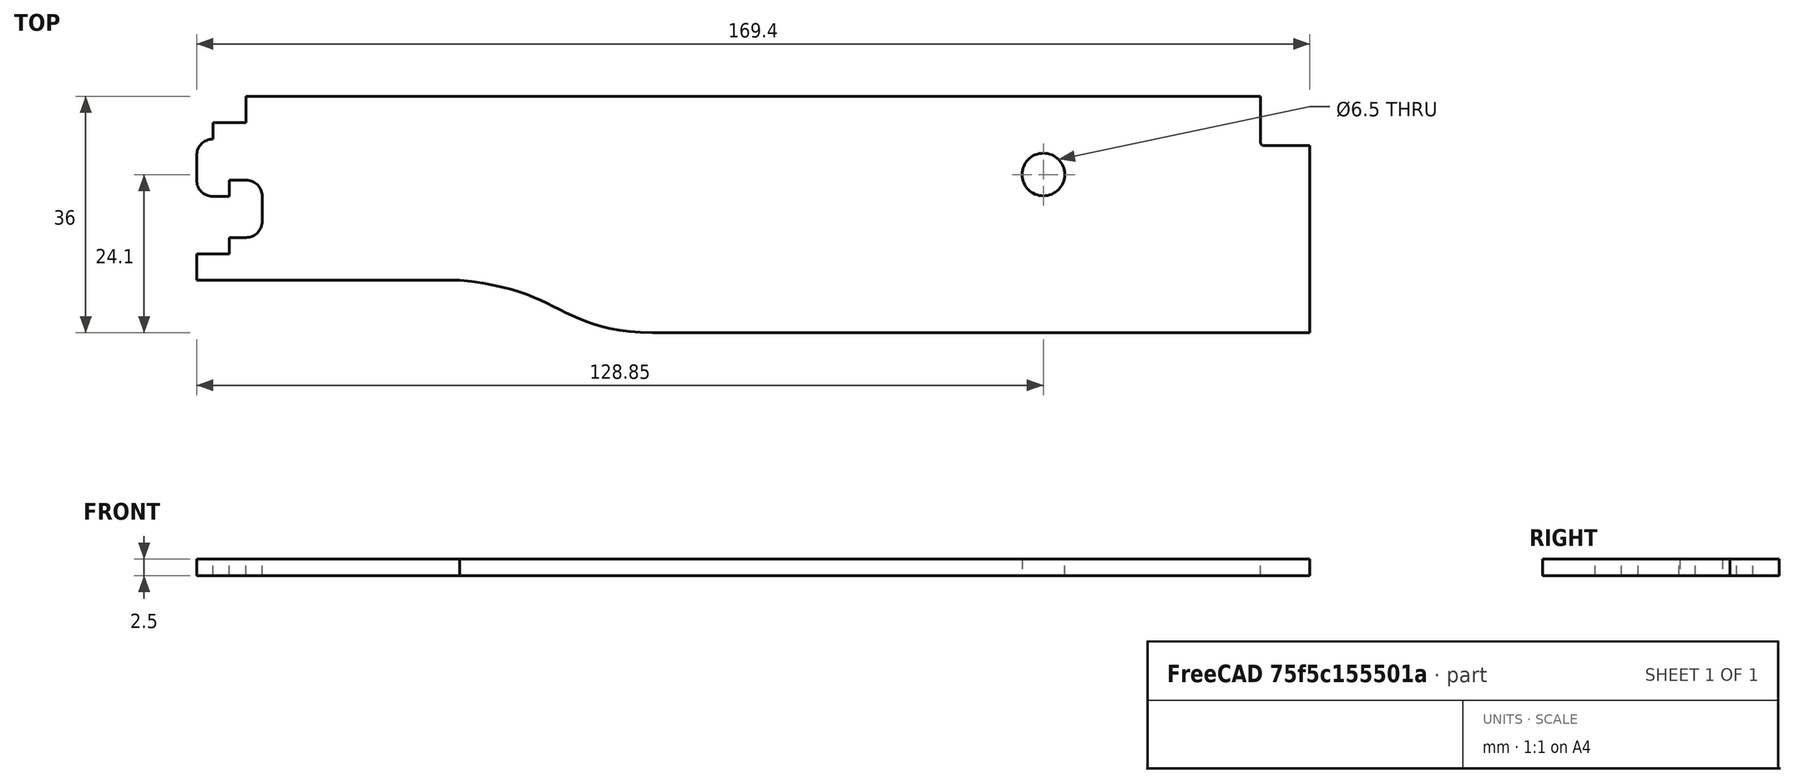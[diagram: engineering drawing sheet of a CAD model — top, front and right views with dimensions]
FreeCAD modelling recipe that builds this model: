
FCSTD DOCUMENT  (FreeCAD 0.19R0.19.2)
Label: v0_14
License: All rights reserved
LicenseURL: http://en.wikipedia.org/wiki/All_rights_reserved
objects: Sketcher::SketchObject×2, Part::Extrusion×1
note: 3 computed .brp shape members not serialized (recipe doc carries the construction recipe); baked Part::Feature solids carry a one-line shape summary decoded from their .brp

FEATURE [Sketcher::SketchObject] Sketch
  FullyConstrained = true
  sketch-geometry (33):
    g0: LineSegment StartX=0 StartY=0 StartZ=0 EndX=154.4 EndY=0 EndZ=0
    g1: LineSegment StartX=154.4 StartY=0 StartZ=0 EndX=154.4 EndY=-7 EndZ=0
    g2: LineSegment StartX=154.9 StartY=-7.5 StartZ=0 EndX=161.9 EndY=-7.5 EndZ=0
    g3: ArcOfCircle CenterX=154.9 CenterY=-7 CenterZ=0 NormalX=0 NormalY=0 NormalZ=1 AngleXU=0 Radius=0.5 StartAngle=3.14159 EndAngle=4.71239
    g4: Circle CenterX=121.35 CenterY=-11.9 CenterZ=0 NormalX=0 NormalY=0 NormalZ=1 AngleXU=0 Radius=3.25
    g5: LineSegment StartX=0 StartY=0 StartZ=0 EndX=0 EndY=-4 EndZ=0
    g6: LineSegment StartX=-5 StartY=-4 StartZ=0 EndX=0 EndY=-4 EndZ=0
    g7: LineSegment StartX=-5 StartY=-4 StartZ=0 EndX=-5 EndY=-6.5 EndZ=0
    g8: LineSegment StartX=-7.5 StartY=-9 StartZ=0 EndX=-7.5 EndY=-12.75 EndZ=0
    g9: ArcOfCircle CenterX=-5 CenterY=-9 CenterZ=0 NormalX=0 NormalY=0 NormalZ=1 AngleXU=0 Radius=2.5 StartAngle=1.5708 EndAngle=3.14159
    g10: LineSegment StartX=-5 StartY=-15.25 StartZ=0 EndX=-2.5 EndY=-15.25 EndZ=0
    g11: ArcOfCircle CenterX=-5 CenterY=-12.75 CenterZ=0 NormalX=0 NormalY=0 NormalZ=1 AngleXU=0 Radius=2.5 StartAngle=3.14159 EndAngle=4.71239
    g12: LineSegment StartX=-2.5 StartY=-15.25 StartZ=0 EndX=-2.5 EndY=-12.75 EndZ=0
    g13: LineSegment StartX=-2.5 StartY=-12.75 StartZ=0 EndX=1.488e-13 EndY=-12.75 EndZ=0
    g14: ArcOfCircle CenterX=1.486e-13 CenterY=-15.25 CenterZ=0 NormalX=0 NormalY=0 NormalZ=1 AngleXU=0 Radius=2.5 StartAngle=8e-16 EndAngle=1.5708
    g15: LineSegment StartX=2.5 StartY=-15.25 StartZ=0 EndX=2.5 EndY=-19 EndZ=0
    g16: ArcOfCircle CenterX=1.483e-13 CenterY=-19 CenterZ=0 NormalX=0 NormalY=0 NormalZ=1 AngleXU=0 Radius=2.5 StartAngle=4.71239 EndAngle=6.28319
    g17: LineSegment StartX=-2.5 StartY=-21.5 StartZ=0 EndX=1.479e-13 EndY=-21.5 EndZ=0
    g18: LineSegment StartX=-2.5 StartY=-21.5 StartZ=0 EndX=-2.5 EndY=-24 EndZ=0
    g19: LineSegment StartX=-7.5 StartY=-24 StartZ=0 EndX=-2.5 EndY=-24 EndZ=0
    g20: LineSegment StartX=-7.5 StartY=-24 StartZ=0 EndX=-7.5 EndY=-28 EndZ=0
    g21: LineSegment StartX=161.9 StartY=-7.5 StartZ=0 EndX=161.9 EndY=-36 EndZ=0
    g22: LineSegment StartX=61.85 StartY=-36 StartZ=0 EndX=161.9 EndY=-36 EndZ=0
    g23-g27: Circle x5 (B-spline internal-alignment scaffolding for g28; pole/knot coordinates omitted)
    g28: BSplineCurve PolesCount=5 KnotsCount=3 Degree=3 IsPeriodic=0
    g29: GeomPoint X=61.85 Y=-36 Z=0
    g30: GeomPoint X=47.2264 Y=-32.2128 Z=0
    g31: GeomPoint X=32.5209 Y=-28 Z=0
    g32: LineSegment StartX=32.5209 StartY=-28 StartZ=0 EndX=-7.5 EndY=-28 EndZ=0
  constraints (75):
    c: PointOnObject(g0,g-2)
    c: Horizontal(g0)
    c: Distance(g0) = 154.4
    c: DistanceY(g-1,g0) = 0
    c: Vertical(g1)
    c: Distance(g1) = 7
    c: Coincident(g1,g0)
    c: Horizontal(g2)
    c: Distance(g2) = 7
    c: Coincident(g3,g1)
    c: Tangent(g2,g3)
    c: Tangent(g2,g3,g2) = -1.5708
    c: Block(g3)
    c: Block(g4)
    c: Vertical(g5)
    c: Distance(g5) = 4
    c: Coincident(g5,g0)
    c: Horizontal(g6)
    c: Distance(g6) = 5
    c: Coincident(g6,g5)
    c: Vertical(g7)
    c: Distance(g7) = 2.5
    c: Coincident(g7,g6)
    c: Vertical(g8)
    c: Distance(g8) = 3.75
    c: Coincident(g9,g7)
    c: Block(g9)
    c: Coincident(g8,g9)
    c: Horizontal(g10)
    c: Distance(g10) = 2.5
    c: Coincident(g11,g8)
    c: Block(g11)
    c: Block(g10)
    c: Vertical(g12)
    c: Distance(g12) = 2.5
    c: Coincident(g12,g10)
    c: Horizontal(g13)
    c: Distance(g13) = 2.5
    c: Coincident(g13,g12)
    c: Coincident(g14,g13)
    c: Vertical(g15)
    c: Distance(g15) = 3.75
    c: Block(g14)
    c: Coincident(g15,g14)
    c: Coincident(g16,g15)
    c: Block(g16)
    c: Horizontal(g17)
    c: Distance(g17) = 2.5
    c: Coincident(g17,g16)
    c: Vertical(g18)
    c: Distance(g18) = 2.5
    c: Coincident(g18,g17)
    c: Horizontal(g19)
    c: Distance(g19) = 5
    c: Coincident(g19,g18)
    c: Vertical(g20)
    c: Distance(g20) = 4
    c: Coincident(g20,g19)
    c: Vertical(g21)
    c: Distance(g21) = 28.5
    c: Coincident(g21,g2)
    c: Horizontal(g22)
    c: Distance(g22) = 100.05
    c: Coincident(g22,g21)
    c: Coincident(g28,g22)
    c: Weight(g23) = 1
    c: Equal(g23, g24-g27) x4
    c: InternalAlignment(g23-g27 -> g28) x5
    c: InternalAlignment(g29,g28)
    c: InternalAlignment(g30,g28)
    c: InternalAlignment(g31,g28)
    c: Horizontal(g32)
    c: Coincident(g32,g20)
    c: Coincident(g32,g28)
    c: Block(g28)
FEATURE [Part::Extrusion] Extrude
  Base = -> Sketch
  Dir = (0,0,1)
  DirMode = 2
  FaceMakerClass = Part::FaceMakerBullseye
  LengthFwd = 2.5
  LengthRev = 0
  Solid = true
  Symmetric = false
FEATURE [Sketcher::SketchObject] Sketch001
  FullyConstrained = true
  sketch-geometry (44):
    g0: LineSegment StartX=0 StartY=0 StartZ=0 EndX=154.4 EndY=0 EndZ=0
    g1: LineSegment StartX=154.4 StartY=0 StartZ=0 EndX=154.4 EndY=-7 EndZ=0
    g2: LineSegment StartX=154.9 StartY=-7.5 StartZ=0 EndX=161.9 EndY=-7.5 EndZ=0
    g3: ArcOfCircle CenterX=154.9 CenterY=-7 CenterZ=0 NormalX=0 NormalY=0 NormalZ=1 AngleXU=0 Radius=0.5 StartAngle=3.14159 EndAngle=4.71239
    g4: LineSegment StartX=0 StartY=0 StartZ=0 EndX=0 EndY=-4 EndZ=0
    g5: LineSegment StartX=-5 StartY=-4 StartZ=0 EndX=0 EndY=-4 EndZ=0
    g6: LineSegment StartX=-5 StartY=-4 StartZ=0 EndX=-5 EndY=-6.5 EndZ=0
    g7: LineSegment StartX=-7.5 StartY=-9 StartZ=0 EndX=-7.5 EndY=-12.75 EndZ=0
    g8: ArcOfCircle CenterX=-5 CenterY=-9 CenterZ=0 NormalX=0 NormalY=0 NormalZ=1 AngleXU=0 Radius=2.5 StartAngle=1.5708 EndAngle=3.14159
    g9: LineSegment StartX=-5 StartY=-15.25 StartZ=0 EndX=-2.5 EndY=-15.25 EndZ=0
    g10: ArcOfCircle CenterX=-5 CenterY=-12.75 CenterZ=0 NormalX=0 NormalY=0 NormalZ=1 AngleXU=0 Radius=2.5 StartAngle=3.14159 EndAngle=4.71239
    g11: LineSegment StartX=-2.5 StartY=-15.25 StartZ=0 EndX=-2.5 EndY=-12.75 EndZ=0
    g12: LineSegment StartX=-2.5 StartY=-12.75 StartZ=0 EndX=1.488e-13 EndY=-12.75 EndZ=0
    g13: ArcOfCircle CenterX=1.486e-13 CenterY=-15.25 CenterZ=0 NormalX=0 NormalY=0 NormalZ=1 AngleXU=0 Radius=2.5 StartAngle=8e-16 EndAngle=1.5708
    g14: LineSegment StartX=2.5 StartY=-15.25 StartZ=0 EndX=2.5 EndY=-19 EndZ=0
    g15: ArcOfCircle CenterX=1.483e-13 CenterY=-19 CenterZ=0 NormalX=0 NormalY=0 NormalZ=1 AngleXU=0 Radius=2.5 StartAngle=4.71239 EndAngle=6.28319
    g16: LineSegment StartX=-2.5 StartY=-21.5 StartZ=0 EndX=1.479e-13 EndY=-21.5 EndZ=0
    g17: LineSegment StartX=-2.5 StartY=-21.5 StartZ=0 EndX=-2.5 EndY=-24 EndZ=0
    g18: LineSegment StartX=-7.5 StartY=-24 StartZ=0 EndX=-2.5 EndY=-24 EndZ=0
    g19: LineSegment StartX=-7.5 StartY=-24 StartZ=0 EndX=-7.5 EndY=-28 EndZ=0
    g20: LineSegment StartX=161.9 StartY=-7.5 StartZ=0 EndX=161.9 EndY=-36 EndZ=0
    g21: LineSegment StartX=61.85 StartY=-36 StartZ=0 EndX=161.9 EndY=-36 EndZ=0
    g22-g26: Circle x5 (B-spline internal-alignment scaffolding for g27; pole/knot coordinates omitted)
    g27: BSplineCurve PolesCount=5 KnotsCount=3 Degree=3 IsPeriodic=0
    g28: GeomPoint X=61.85 Y=-36 Z=0
    g29: GeomPoint X=47.2264 Y=-32.2128 Z=0
    g30: GeomPoint X=32.5209 Y=-28 Z=0
    g31: LineSegment StartX=32.5209 StartY=-28 StartZ=0 EndX=-7.5 EndY=-28 EndZ=0
    g32: ArcOfCircle CenterX=144.4 CenterY=-26 CenterZ=0 NormalX=0 NormalY=0 NormalZ=1 AngleXU=0 Radius=5 StartAngle=4.71239 EndAngle=6.28319
    g33: ArcOfCircle CenterX=144.4 CenterY=-10 CenterZ=0 NormalX=0 NormalY=0 NormalZ=1 AngleXU=0 Radius=5 StartAngle=0 EndAngle=1.5708
    g34: LineSegment StartX=149.4 StartY=-10 StartZ=0 EndX=149.4 EndY=-26 EndZ=0
    g35: LineSegment StartX=104.85 StartY=-31 StartZ=0 EndX=144.4 EndY=-31 EndZ=0
    g36: LineSegment StartX=104.85 StartY=-31 StartZ=0 EndX=104.85 EndY=-34.5 EndZ=0
    g37: LineSegment StartX=54.35 StartY=-34.5 StartZ=0 EndX=104.85 EndY=-34.5 EndZ=0
    g38: LineSegment StartX=54.35 StartY=-23 StartZ=0 EndX=54.35 EndY=-34.5 EndZ=0
    g39: LineSegment StartX=20 StartY=-23 StartZ=0 EndX=54.35 EndY=-23 EndZ=0
    g40: ArcOfCircle CenterX=20 CenterY=-18 CenterZ=0 NormalX=0 NormalY=0 NormalZ=1 AngleXU=0 Radius=5 StartAngle=3.14159 EndAngle=4.71239
    g41: ArcOfCircle CenterX=20 CenterY=-10 CenterZ=0 NormalX=0 NormalY=0 NormalZ=1 AngleXU=0 Radius=5 StartAngle=1.5708 EndAngle=3.14159
    g42: LineSegment StartX=20 StartY=-5 StartZ=0 EndX=144.4 EndY=-5 EndZ=0
    g43: LineSegment StartX=15 StartY=-10 StartZ=0 EndX=15 EndY=-18 EndZ=0
  constraints (102):
    c: PointOnObject(g0,g-2)
    c: Horizontal(g0)
    c: Distance(g0) = 154.4
    c: DistanceY(g-1,g0) = 0
    c: Vertical(g1)
    c: Distance(g1) = 7
    c: Coincident(g1,g0)
    c: Horizontal(g2)
    c: Distance(g2) = 7
    c: Coincident(g3,g1)
    c: Tangent(g2,g3)
    c: Tangent(g2,g3,g2) = -1.5708
    c: Block(g3)
    c: Vertical(g4)
    c: Distance(g4) = 4
    c: Coincident(g4,g0)
    c: Horizontal(g5)
    c: Distance(g5) = 5
    c: Coincident(g5,g4)
    c: Vertical(g6)
    c: Distance(g6) = 2.5
    c: Coincident(g6,g5)
    c: Vertical(g7)
    c: Distance(g7) = 3.75
    c: Coincident(g8,g6)
    c: Block(g8)
    c: Coincident(g7,g8)
    c: Horizontal(g9)
    c: Distance(g9) = 2.5
    c: Coincident(g10,g7)
    c: Block(g10)
    c: Block(g9)
    c: Vertical(g11)
    c: Distance(g11) = 2.5
    c: Coincident(g11,g9)
    c: Horizontal(g12)
    c: Distance(g12) = 2.5
    c: Coincident(g12,g11)
    c: Coincident(g13,g12)
    c: Vertical(g14)
    c: Distance(g14) = 3.75
    c: Block(g13)
    c: Coincident(g14,g13)
    c: Coincident(g15,g14)
    c: Block(g15)
    c: Horizontal(g16)
    c: Distance(g16) = 2.5
    c: Coincident(g16,g15)
    c: Vertical(g17)
    c: Distance(g17) = 2.5
    c: Coincident(g17,g16)
    c: Horizontal(g18)
    c: Distance(g18) = 5
    c: Coincident(g18,g17)
    c: Vertical(g19)
    c: Distance(g19) = 4
    c: Coincident(g19,g18)
    c: Vertical(g20)
    c: Distance(g20) = 28.5
    c: Coincident(g20,g2)
    c: Horizontal(g21)
    c: Distance(g21) = 100.05
    c: Coincident(g21,g20)
    c: Coincident(g27,g21)
    c: Weight(g22) = 1
    c: Equal(g22, g23-g26) x4
    c: InternalAlignment(g22-g26 -> g27) x5
    c: InternalAlignment(g28,g27)
    c: InternalAlignment(g29,g27)
    c: InternalAlignment(g30,g27)
    c: Horizontal(g31)
    c: Coincident(g31,g19)
    c: Coincident(g31,g27)
    c: Block(g27)
    c: Block(g32)
    c: Block(g33)
    c: Vertical(g34)
    c: Coincident(g34,g33)
    c: Coincident(g34,g32)
    c: Horizontal(g35)
    c: Coincident(g35,g32)
    c: Block(g35)
    c: Vertical(g36)
    c: Distance(g36) = 3.5
    c: Coincident(g36,g35)
    c: Horizontal(g37)
    c: Coincident(g37,g36)
    c: Distance(g37) = 50.5
    c: Block(g37)
    c: Coincident(g38,g37)
    c: Vertical(g38)
    c: Distance(g38) = 11.5
    c: Horizontal(g39)
    c: Coincident(g39,g38)
    c: Block(g40)
    c: Block(g39)
    c: Block(g41)
    c: Horizontal(g42)
    c: Coincident(g42,g41)
    c: Coincident(g42,g33)
    c: Coincident(g43,g41)
    c: Coincident(g43,g40)
